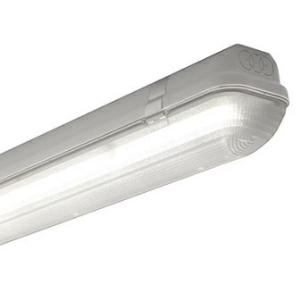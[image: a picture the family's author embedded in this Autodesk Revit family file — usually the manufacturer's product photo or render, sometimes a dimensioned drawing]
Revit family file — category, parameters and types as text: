
# Revit family: 3f_filippi_-_3f_linda_3f_filippi_-_58592_-_3f_linda_led_1x18w_ep_l1270
name_source: partatom
category: Lighting Fixtures
units: mm (PartAtom-declared; Revit-internal decimal feet)

## family parameters
Cut with Voids When Loaded = No
Host = Face
Light Source = No
Part Type = Normal
Room Calculation Point = No
Round Connector Dimension = Use Diameter
Shared = No

## types (1)
- 3F Filippi - 3F Linda (1 x LED, 2967 lm, 21 W, 4000 K)
    Apparent Load = 21 VA
    Approval mark = ENEC
    CIE Flux Codes = 44 77 94 97 100
    Color Rendering = 80
    Color Temperature = 4000 K
    Control Gear = Electronic ballast
    Default Elevation = 1800 mm
    Description = ILLUMINOTECHNICAL
Luminous efficiency 100% (DLOR 97%, ULOR 3%).
Initial luminous flux of the luminaire 2967 lm.
Emergency luminaire luminous flux BLF 18%.
Controlled symmetric distribution.
Installation Interdistance Transv.D = 1.77 x hu - Long.D = 1.17 x hu.
Tabular UGR (CIE 117 - 4H-8H; S=0.25H; 70/50/20): RUG 20.9 - 21.8.
Beam angle: 109° - 64°.
Luminous efficacy 141 lm/W.
Lifetime (L93/B10): 30000 h. (tq+25°C)
Lifetime (L90/B10): 50000 h. (tq+25°C)
Lifetime (L85/B10): 80000 h. (tq+25°C)
Lifetime (L80/B10): 100000 h. (tq+25°C)
Sudden decreased luminous flux after 50000 hours: 0% (C0).
Photobiological safety in compliance with IEC/TR 62778: RG0 risk exempt, (IEC 62471).
In compliance with IEC/EN 62722-2-1 - IEC/EN 62717 standards.

SOURCE
Linear LED module 18W/840.
Energy efficiency class (UE 2019/2020 - UE 2019/2015): D.
CIE 13.3 Colour rendering index: CRI >80 (R9 <50%).
IES TM-30 Fidelity Index: Rf = 84 Rg = 95.
CCT nominal colour temperature 4000 K.
Colour initial tolerance (MacAdam): SDCM 3.

MECHANICAL
Self-extinguishing V2 polycarbonate housing, injection moulded, RAL 7035 grey.
Ecologic anti-aging injected sealing gasket.
Diffuser in self-extinguishing V2 polycarbonate, photo-engraved interior, UV stabilised, injection moulded with smooth outer surface, tamper-proof opening.
Gear-holder reflector in hot-dip galvanised steel, painted with white polyester base.
Snug fit safety snap-lock clips for diffuser mounting in stainless steel, screwdriver opening.
Fixing brackets in stainless steel.
Possibility for technicians to access the interior of the luminaire.
Luminaire with limited surface temperature. - D - (EN 60598-2-24)
Dimensions: 1270x100 mm, height 100 mm. Weight 2.95 kg.
IP66 protection degree.
Mechanical strength to impacts IK10 (20 joule).
Glow-wire test resistance 850°C.

ELECTRICAL
Halogen Free electronic wiring 230V-50/60Hz, power factor 0.90, THD <25%, constant output current, SELV, class I, 1 driver.
Power of the luminaire 21 W.
CE - IEC 60598-1 - EN 60598-1.
EP maintained emergency wiring on board, 1h duration, 24h recharge; compliant with EN 60598-2-22, excluding high risk areas.
SAFE FLICKER: PstLM=<1 and SVM=<0.4 (IEC TR 61547-1 and IEC TR 63158), to ensure a more comfortable and safe light.
Ambient temperature from +5°C to +25°C.
Temperature class T6 max 85°C.
Relative humidity UR: <85%.

INSTALLATION
Ceiling / Suspended / Wall.
All accessories dedicated to this product are available on the Catalog and on our website www.3F-Filippi.com.

APPLICATIONS
Suitable product for food production plants (HACCP), IFS (Food Version 6), BRC (GSFS Food Version 7).
Dry, dusty indoor environments, subject to occasional water splashes.
Virtually shatterproof polycarbonate compatibly with the fumes / atmospheres that compromise the elasticity of plastic materials.
Not suitable for installation on surfaces subject to important vibrations, exposed to weather conditions, on ropes or poles.
Suitable for illumination of public car parks and parking grounds referred to DIN 67528:2018-04.

WARNING
Fixture not suitable for cold stores with an ambient temperature <5°C and/or relative humidity >85%.
Luminaire designed for disposal/recycling at end-of-life.
Replaceable (LED only) light source by a professional. Replaceable control gear by a professional.
    Height = 100 mm  [stored 0.328084 ft]
    Lamp = 1 x LED
    Lamp Light Flux = 2967 lm
    Lamp Power = 21 W
    Lamp count = 1
    Length = 1270 mm
    Lifetime = 50000 h
    Luminous efficacy = 141 lm/W
    Manufacturer = 3F Filippi
    ModVariant = No
    Model = 3F Filippi - 58592 - 3F Linda LED 1x18W EP L1270
    Mounting Place = Ceiling
    Mounting Type = Pendant
    Number of Poles = 1
    OnlyDefault = Yes
    Power Factor = 1
    Product Name = 3F Filippi - 3F Linda
    Product group = pendant luminaire
    ProductGroupID = 9
    Protection Class = Protection class I
    Protection Degree = IP 66
    RLX_Detail_Level = 1
    RLX_Emergency_Light_Flux = 0 lm
    RLX_Emergency_Type = 0
    RLX_Emergency_Type_DB = No
    RlxData = <blob elided: 68817 chars, md5=16140c15>
    Socket = socket
    Standby Power = 0 W
    System Light Flux = 2967 lm
    System Power = 21 W
    Type Comments = Product without accessories
    Type Image = 3ffilippi_3f_linda_led_1x.jpg
    URL = http://relux.com
    VarID = ---
    Voltage = 0 V
    Weight = 0.00 kg
    Width = 100 mm  [stored 0.328084 ft]

note: [stored X ft] marks values corroborated as IEEE doubles in the binary element streams (Revit-internal decimal feet)

## geometry (parser evidence)
native form markers: Blend x4, Sweep x10
no freeform markers — native parametric forms only
